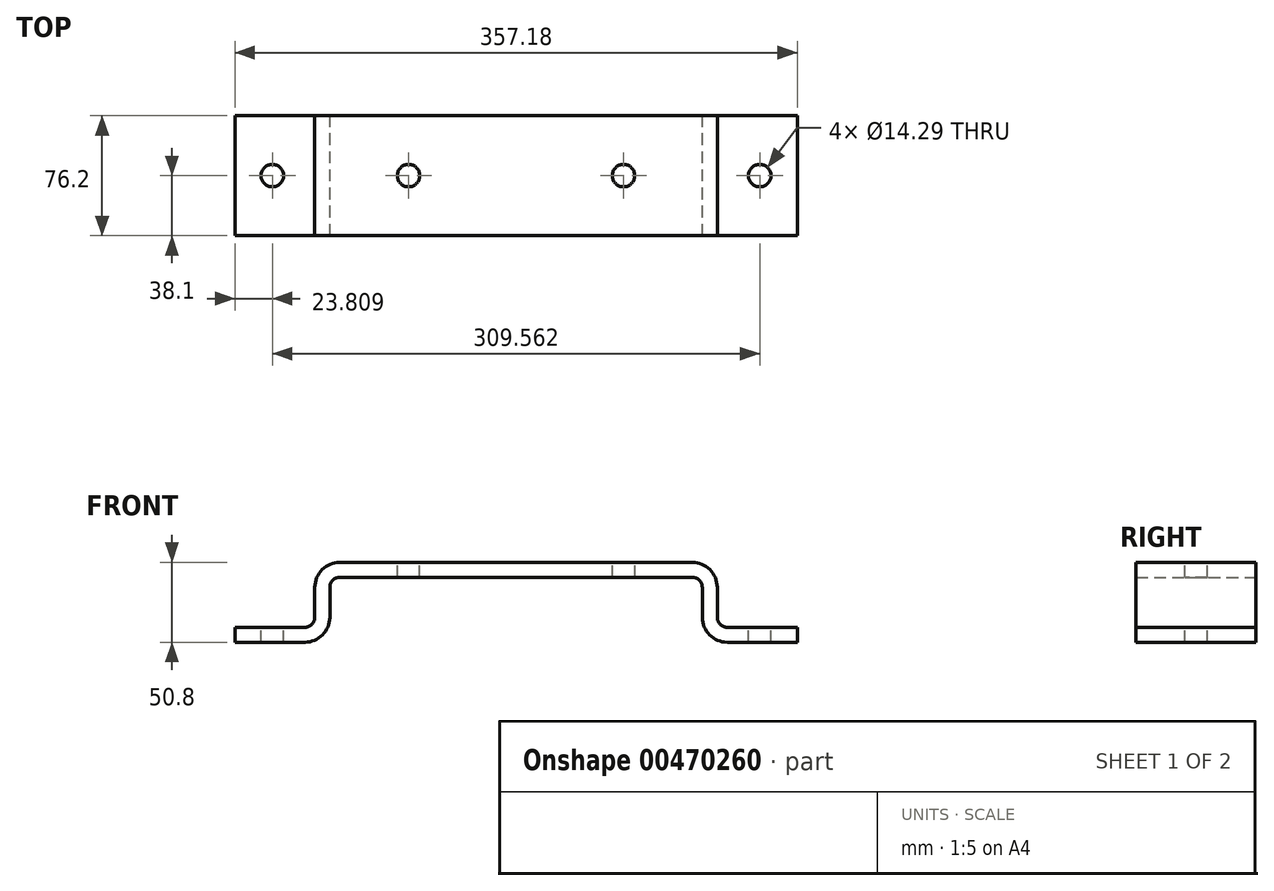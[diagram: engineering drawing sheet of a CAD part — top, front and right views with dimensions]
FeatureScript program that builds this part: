
annotation { "Feature Type Name" : "Feature", "Feature Type Description" : "" }
export const myFeature = defineFeature(function(context is Context, id is Id, definition is map)
    precondition{}
    {
        {
            var Q0;
            Q0=qCreatedBy(makeId("Front.planeOp"),FACE);
            var sketch = newSketch(context, id + "F0", { "sketchPlane" : qUnion([Q0])});
            skLineSegment(sketch, "E0.bottom", {"start": v(-178.6, -25.4) * mm, "end": v(-118.27, -25.4) * mm});
            skLineSegment(sketch, "E0.top", {"start": v(-127.8, 25.4) * mm, "end": v(127.8, 25.4) * mm});
            skLineSegment(sketch, "E0.left", {"start": v(-178.6, -25.4) * mm, "end": v(-178.6, -15.88) * mm});
            skLineSegment(sketch, "E0.right", {"start": v(178.6, -25.4) * mm, "end": v(178.6, -15.88) * mm});
            skPoint(sketch, "E0.middle", {"position": v(0, 0) * mm});
            skLineSegment(sketch, "E1.0", {"start": v(-178.6, -15.88) * mm, "end": v(-127.8, -15.88) * mm});
            skLineSegment(sketch, "E2.0", {"start": v(127.8, -15.88) * mm, "end": v(127.8, 25.4) * mm});
            skLineSegment(sketch, "E3.0", {"start": v(118.27, -25.4) * mm, "end": v(118.27, 15.88) * mm});
            skLineSegment(sketch, "E4.0", {"start": v(-127.8, -15.88) * mm, "end": v(-127.8, 25.4) * mm});
            skLineSegment(sketch, "E5.0", {"start": v(-118.27, -25.4) * mm, "end": v(-118.27, 15.87) * mm});
            skLineSegment(sketch, "E6.0", {"start": v(-118.27, 15.88) * mm, "end": v(118.27, 15.88) * mm});
            skPoint(sketch, "E7.orphan", {"position": v(-178.6, 25.4) * mm});
            skLineSegment(sketch, "E8.trimOffspring", {"start": v(127.8, -15.88) * mm, "end": v(178.6, -15.88) * mm});
            skLineSegment(sketch, "E9.trimOffspring", {"start": v(118.27, -25.4) * mm, "end": v(178.6, -25.4) * mm});
            skPoint(sketch, "E10.orphan", {"position": v(178.6, 25.4) * mm});
            skSolve(sketch);
        }
        {
            var Q0;
            Q0=qSketchRegion(id+"F0",true);
            extrude(context, id + "F1", {"entities" : qUnion([Q0]), "endBound" : BoundingType.SYMMETRIC, "depth" : 76.2 * mm});
        }
        {
            var Q0;
            Q0=makeQuery(id+"F1.opExtrude","SWEPT_EDGE",EDGE,{"disambiguationData":[OSD([sQuery(id+"F0.wireOp",EDGE,"E1.0"),sQuery(id+"F0.wireOp",EDGE,"E4.0")])]});
            var Q1;
            Q1=makeQuery(id+"F1.opExtrude","SWEPT_EDGE",EDGE,{"disambiguationData":[OSD([sQuery(id+"F0.wireOp",EDGE,"E5.0"),sQuery(id+"F0.wireOp",EDGE,"E6.0")])]});
            var Q2;
            Q2=makeQuery(id+"F1.opExtrude","SWEPT_EDGE",EDGE,{"disambiguationData":[OSD([sQuery(id+"F0.wireOp",EDGE,"E3.0"),sQuery(id+"F0.wireOp",EDGE,"E6.0")])]});
            var Q3;
            Q3=makeQuery(id+"F1.opExtrude","SWEPT_EDGE",EDGE,{"disambiguationData":[OSD([sQuery(id+"F0.wireOp",EDGE,"E2.0"),sQuery(id+"F0.wireOp",EDGE,"E8.trimOffspring")])]});
            fillet(context, id + "F2", {"entities" : qUnion([Q0, Q1, Q2, Q3]), "radius" : 6.35 * mm, "tangentPropagation" : true, "allowEdgeOverflow" : false});
        }
        {
            var Q0;
            Q0=makeQuery(id+"F1.opExtrude","SWEPT_EDGE",EDGE,{"disambiguationData":[OSD([sQuery(id+"F0.wireOp",EDGE,"E0.top"),sQuery(id+"F0.wireOp",EDGE,"E4.0")])]});
            var Q1;
            Q1=makeQuery(id+"F1.opExtrude","SWEPT_EDGE",EDGE,{"disambiguationData":[OSD([sQuery(id+"F0.wireOp",EDGE,"E0.top"),sQuery(id+"F0.wireOp",EDGE,"E2.0")])]});
            var Q2;
            Q2=makeQuery(id+"F1.opExtrude","SWEPT_EDGE",EDGE,{"disambiguationData":[OSD([sQuery(id+"F0.wireOp",EDGE,"E3.0"),sQuery(id+"F0.wireOp",EDGE,"E9.trimOffspring")])]});
            var Q3;
            Q3=makeQuery(id+"F1.opExtrude","SWEPT_EDGE",EDGE,{"disambiguationData":[OSD([sQuery(id+"F0.wireOp",EDGE,"E0.bottom"),sQuery(id+"F0.wireOp",EDGE,"E5.0")])]});
            fillet(context, id + "F3", {"entities" : qUnion([Q0, Q1, Q2, Q3]), "radius" : 15.88 * mm, "tangentPropagation" : true, "allowEdgeOverflow" : false});
        }
        {
            var Q0;
            Q0=makeQuery(id+"F1.opExtrude","SWEPT_FACE",FACE,{"disambiguationData":[OSD([sQuery(id+"F0.wireOp",EDGE,"E0.top")])]});
            var sketch = newSketch(context, id + "F4", { "sketchPlane" : qUnion([Q0])});
            skCircle(sketch, "E11", {"center": v(-68.26, 0) * mm, "radius": 7.14 * mm});
            skCircle(sketch, "E12.MirrorC", {"center": v(68.26, 0) * mm, "radius": 7.14 * mm});
            skSolve(sketch);
        }
        {
            var Q0;
            Q0=qSketchRegion(id+"F4",true);
            extrude(context, id + "F5", {"entities" : qUnion([Q0]), "operationType" : NewBodyOperationType.REMOVE, "oppositeDirection" : true, "depth" : 25.4 * mm});
        }
        {
            var Q0;
            Q0=makeQuery(id+"F1.opExtrude","SWEPT_FACE",FACE,{"disambiguationData":[OSD([sQuery(id+"F0.wireOp",EDGE,"E1.0")])]});
            var sketch = newSketch(context, id + "F6", { "sketchPlane" : qUnion([Q0])});
            skCircle(sketch, "E13", {"center": v(-154.78, 0) * mm, "radius": 7.14 * mm});
            skCircle(sketch, "E14.MirrorC", {"center": v(154.78, 0) * mm, "radius": 7.14 * mm});
            skSolve(sketch);
        }
        {
            var Q0;
            Q0=qSketchRegion(id+"F6",true);
            extrude(context, id + "F7", {"entities" : qUnion([Q0]), "operationType" : NewBodyOperationType.REMOVE, "oppositeDirection" : true, "depth" : 25.4 * mm});
        }
    });
